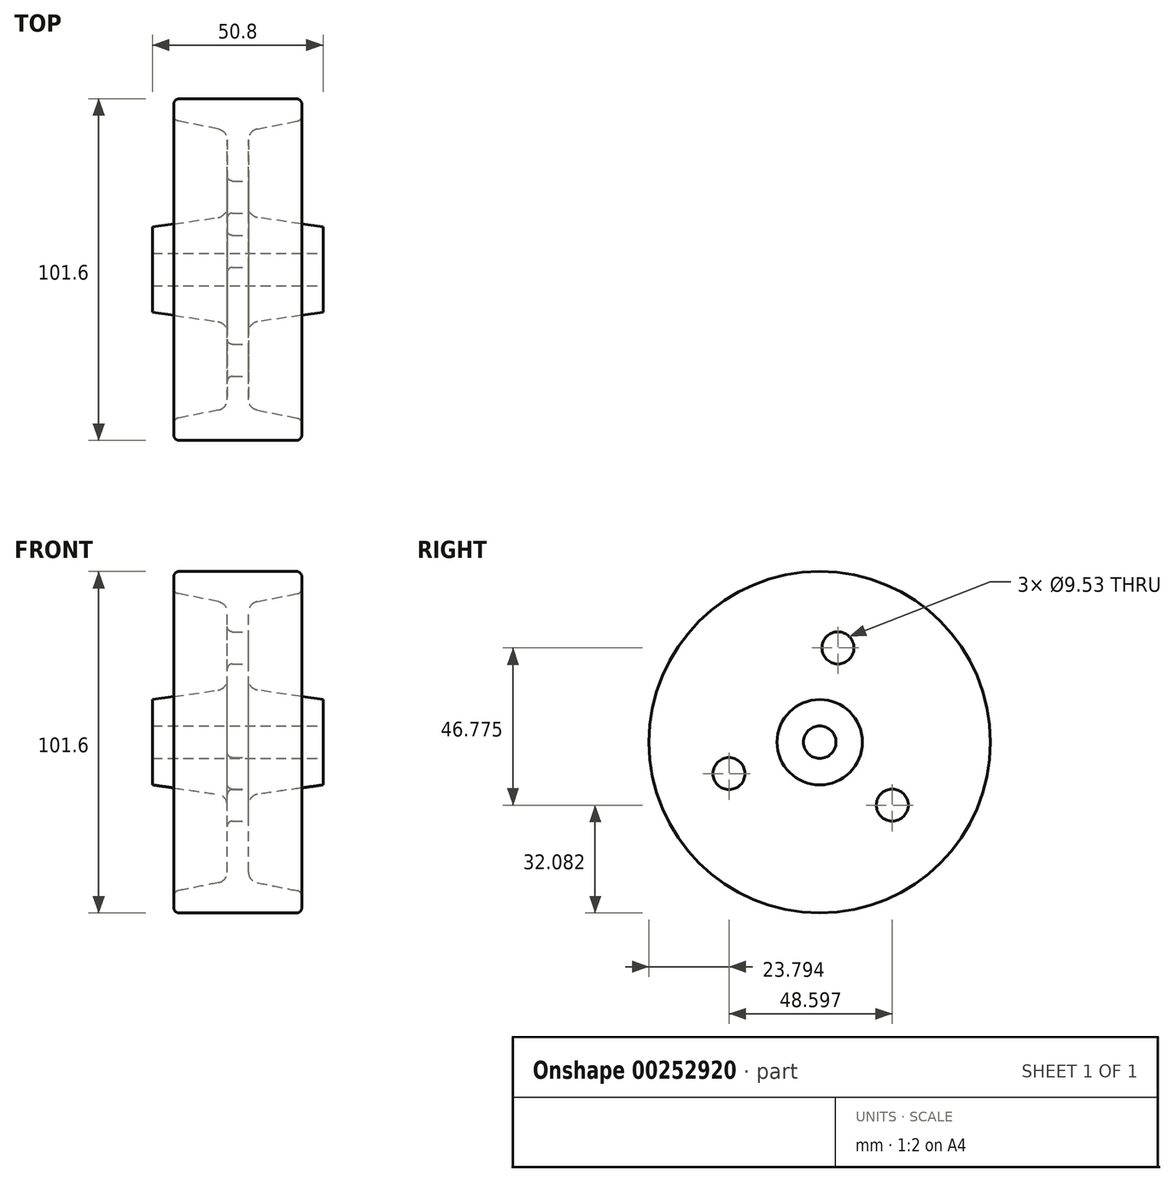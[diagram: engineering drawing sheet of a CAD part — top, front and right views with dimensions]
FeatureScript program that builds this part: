
annotation { "Feature Type Name" : "Feature", "Feature Type Description" : "" }
export const myFeature = defineFeature(function(context is Context, id is Id, definition is map)
    precondition{}
    {
        {
            var Q0;
            Q0=qCreatedBy(makeId("Front.planeOp"),FACE);
            var sketch = newSketch(context, id + "F0", { "sketchPlane" : qUnion([Q0])});
            skLineSegment(sketch, "E0", {"start": v(0, 0) * mm, "end": v(0, 50.8) * mm, "construction": true});
            skLineSegment(sketch, "E1", {"start": v(0, 50.8) * mm, "end": v(-17.46, 50.8) * mm});
            skLineSegment(sketch, "E2", {"start": v(-19.05, 49.21) * mm, "end": v(-19.05, 45.75) * mm});
            skLineSegment(sketch, "E3", {"start": v(0, 0) * mm, "end": v(-3.18, 0) * mm});
            skLineSegment(sketch, "E4", {"start": v(-3.18, 18.63) * mm, "end": v(-3.18, 38.67) * mm});
            skLineSegment(sketch, "E5", {"start": v(-5.73, 41.79) * mm, "end": v(-17.77, 44.2) * mm});
            skLineSegment(sketch, "E6", {"start": v(-3.18, 0) * mm, "end": v(-25.4, 0) * mm});
            skLineSegment(sketch, "E7", {"start": v(-25.4, 0) * mm, "end": v(-25.4, 12.7) * mm});
            skPoint(sketch, "E8.visualSharp", {"position": v(-3.18, 41.28) * mm});
            skArc(sketch, "E8.filletArc", {"start": v(-3.18, 38.67) * mm, "mid": v(-3.9, 40.69) * mm, "end": v(-5.73, 41.79) * mm});
            skPoint(sketch, "E9.visualSharp", {"position": v(-19.05, 44.45) * mm});
            skArc(sketch, "E9.filletArc", {"start": v(-19.05, 45.75) * mm, "mid": v(-18.7, 44.74) * mm, "end": v(-17.77, 44.2) * mm});
            skPoint(sketch, "E10.visualSharp", {"position": v(-19.05, 50.8) * mm});
            skArc(sketch, "E10.filletArc", {"start": v(-17.46, 50.8) * mm, "mid": v(-18.59, 50.34) * mm, "end": v(-19.05, 49.21) * mm});
            skLineSegment(sketch, "E11", {"start": v(-25.4, 12.7) * mm, "end": v(-5.9, 15.49) * mm});
            skPoint(sketch, "E12.visualSharp", {"position": v(-3.18, 15.88) * mm});
            skArc(sketch, "E12.filletArc", {"start": v(-5.9, 15.49) * mm, "mid": v(-3.95, 16.55) * mm, "end": v(-3.18, 18.63) * mm});
            skLineSegment(sketch, "E13", {"start": v(-3.18, 15.88) * mm, "end": v(-3.18, 0) * mm, "construction": true});
            skArc(sketch, "E14.MirrorCS", {"start": v(17.46, 50.8) * mm, "mid": v(18.59, 50.34) * mm, "end": v(19.05, 49.21) * mm});
            skArc(sketch, "E15.MirrorCS", {"start": v(19.05, 45.75) * mm, "mid": v(18.7, 44.74) * mm, "end": v(17.77, 44.2) * mm});
            skLineSegment(sketch, "E16.MirrorCS", {"start": v(0, 0) * mm, "end": v(3.18, 0) * mm});
            skLineSegment(sketch, "E17.MirrorCS", {"start": v(19.05, 49.21) * mm, "end": v(19.05, 45.75) * mm});
            skArc(sketch, "E18.MirrorCS", {"start": v(5.9, 15.49) * mm, "mid": v(3.95, 16.55) * mm, "end": v(3.18, 18.63) * mm});
            skArc(sketch, "E19.MirrorCS", {"start": v(3.18, 38.67) * mm, "mid": v(3.9, 40.69) * mm, "end": v(5.73, 41.79) * mm});
            skLineSegment(sketch, "E20.MirrorCS", {"start": v(25.4, 12.7) * mm, "end": v(5.9, 15.49) * mm});
            skLineSegment(sketch, "E21.MirrorCS", {"start": v(25.4, 0) * mm, "end": v(25.4, 12.7) * mm});
            skLineSegment(sketch, "E22.MirrorCS", {"start": v(3.18, 0) * mm, "end": v(25.4, 0) * mm});
            skPoint(sketch, "E23.MirrorP", {"position": v(19.05, 50.8) * mm});
            skLineSegment(sketch, "E24.MirrorCS", {"start": v(5.73, 41.79) * mm, "end": v(17.77, 44.2) * mm});
            skLineSegment(sketch, "E25.MirrorCS", {"start": v(3.18, 18.63) * mm, "end": v(3.18, 38.67) * mm});
            skPoint(sketch, "E26.MirrorP", {"position": v(3.18, 15.88) * mm});
            skLineSegment(sketch, "E27.MirrorCS", {"start": v(0, 50.8) * mm, "end": v(17.46, 50.8) * mm});
            skLineSegment(sketch, "E28.MirrorCS", {"start": v(3.18, 15.88) * mm, "end": v(3.18, 0) * mm, "construction": true});
            skPoint(sketch, "E29.MirrorP", {"position": v(3.18, 41.28) * mm});
            skPoint(sketch, "E30.MirrorP", {"position": v(19.05, 44.45) * mm});
            skSolve(sketch);
        }
        {
            var Q0;
            Q0=qCreatedBy(makeId("Right.planeOp"),FACE);
            var sketch = newSketch(context, id + "F1", { "sketchPlane" : qUnion([Q0])});
            skCircle(sketch, "E31", {"center": v(0, 0) * mm, "radius": 4.83 * mm});
            skCircle(sketch, "E32.cCircle", {"center": v(0, 0) * mm, "radius": 28.58 * mm, "construction": true});
            skLineSegment(sketch, "E32.0", {"start": v(5.41, 28.06) * mm, "end": v(21.6, -18.72) * mm, "construction": true});
            skLineSegment(sketch, "E32.1", {"start": v(21.6, -18.72) * mm, "end": v(-27, -9.34) * mm, "construction": true});
            skLineSegment(sketch, "E32.2", {"start": v(-27, -9.34) * mm, "end": v(5.41, 28.06) * mm, "construction": true});
            skCircle(sketch, "E33", {"center": v(5.41, 28.06) * mm, "radius": 4.76 * mm});
            skCircle(sketch, "E34", {"center": v(-27, -9.34) * mm, "radius": 4.76 * mm});
            skCircle(sketch, "E35", {"center": v(21.6, -18.72) * mm, "radius": 4.76 * mm});
            skSolve(sketch);
        }
        {
            var Q0;
            Q0 = qSketchRegion(id + "F0", true);
            var Q1;
            Q1 = qConstructionFilter(qBodyType(qCreatedBy(id + "F0" ,EDGE), BodyType.WIRE), ConstructionObject.NO);
            var Q2;
            Q2=sQuery(id+"F0.wireOp",EDGE,"E6");
            revolve(context, id + "F2", {"entities" : qUnion([Q0]), "surfaceEntities" : qUnion([Q1]), "axis" : qUnion([Q2]), "revolveType" : RevolveType.FULL});
        }
        {
            var Q0;
            Q0 = qSketchRegion(id + "F1", true);
            extrude(context, id + "F3", {"entities" : qUnion([Q0]), "operationType" : NewBodyOperationType.REMOVE, "oppositeDirection" : true, "depth" : 25.4 * mm, "hasSecondDirection" : true, "secondDirectionOppositeDirection" : false, "secondDirectionDepth" : 25.4 * mm});
        }
        {
            var Q0;
            Q0=makeQuery(id+"F3.boolean.opBoolean","INTERSECT",EDGE,{"derivedFrom":[makeQuery(id+"F2.opRevolve","SWEPT_FACE",FACE,{"disambiguationData":[OSD([sQuery(id+"F0.wireOp",EDGE,"E4")])]}),makeQuery(id+"F3.opExtrude","SWEPT_FACE",FACE,{"disambiguationData":[OSD([sQuery(id+"F1.wireOp",EDGE,"E33")])]})]});
            var Q1;
            Q1=makeQuery(id+"F3.boolean.opBoolean","INTERSECT",EDGE,{"derivedFrom":[makeQuery(id+"F2.opRevolve","SWEPT_FACE",FACE,{"disambiguationData":[OSD([sQuery(id+"F0.wireOp",EDGE,"E4")])]}),makeQuery(id+"F3.opExtrude","SWEPT_FACE",FACE,{"disambiguationData":[OSD([sQuery(id+"F1.wireOp",EDGE,"E34")])]})]});
            var Q2;
            Q2=makeQuery(id+"F3.boolean.opBoolean","INTERSECT",EDGE,{"derivedFrom":[makeQuery(id+"F2.opRevolve","SWEPT_FACE",FACE,{"disambiguationData":[OSD([sQuery(id+"F0.wireOp",EDGE,"E4")])]}),makeQuery(id+"F3.opExtrude","SWEPT_FACE",FACE,{"disambiguationData":[OSD([sQuery(id+"F1.wireOp",EDGE,"E35")])]})]});
            fillet(context, id + "F4", {"entities" : qUnion([Q0, Q1, Q2]), "radius" : 1.59 * mm, "tangentPropagation" : true, "allowEdgeOverflow" : false});
        }
    });
